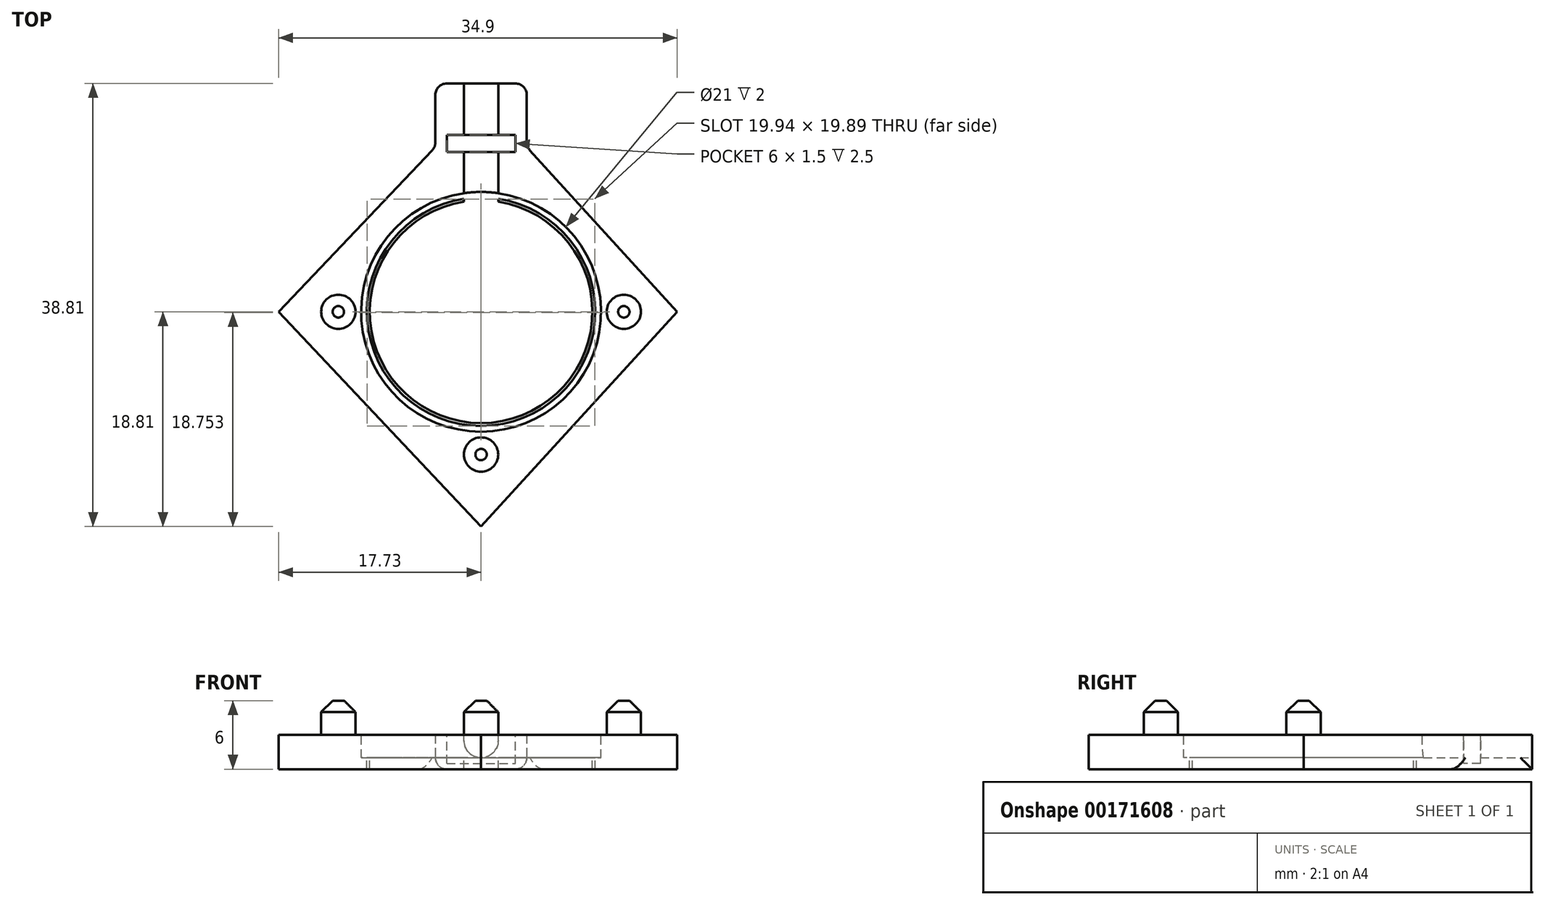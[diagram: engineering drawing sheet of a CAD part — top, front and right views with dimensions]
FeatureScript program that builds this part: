
annotation { "Feature Type Name" : "Feature", "Feature Type Description" : "" }
export const myFeature = defineFeature(function(context is Context, id is Id, definition is map)
    precondition{}
    {
        {
            var Q0;
            Q0=qCreatedBy(makeId("Top.planeOp"),FACE);
            var sketch = newSketch(context, id + "F0", { "sketchPlane" : qUnion([Q0])});
            skLineSegment(sketch, "E0.bottom", {"start": v(-4, 20) * mm, "end": v(4, 20) * mm});
            skLineSegment(sketch, "E0.left", {"start": v(-4, 20) * mm, "end": v(-4, 14.46) * mm});
            skLineSegment(sketch, "E0.right", {"start": v(4, 20) * mm, "end": v(4, 14.46) * mm});
            skLineSegment(sketch, "E1", {"start": v(-4, 14.46) * mm, "end": v(-17.73, 0) * mm});
            skLineSegment(sketch, "E2", {"start": v(4, 14.46) * mm, "end": v(17.17, 0) * mm});
            skLineSegment(sketch, "E3", {"start": v(0, 0) * mm, "end": v(0, -18.81) * mm});
            skLineSegment(sketch, "E4", {"start": v(0, -18.81) * mm, "end": v(-17.73, 0) * mm});
            skLineSegment(sketch, "E5", {"start": v(0, -18.81) * mm, "end": v(17.17, 0) * mm});
            skSolve(sketch);
        }
        {
            var Q0;
            Q0=qSketchRegion(id+"F0",true);
            extrude(context, id + "F1", {"entities" : qUnion([Q0]), "depth" : 3 * mm});
        }
        {
            var Q0;
            Q0=makeQuery(id+"F1.opExtrude","CAP_FACE",FACE,{"disambiguationData":[OSD([sQuery(id+"F0.wireOp",EDGE,"9GDV016W-EE9P-wzn8-Ccm6-bac6Yka38ORT"),sQuery(id+"F0.wireOp",EDGE,"E0.bottom"),sQuery(id+"F0.wireOp",EDGE,"E0.left"),sQuery(id+"F0.wireOp",EDGE,"E0.right")])],"isStart":false});
            var sketch = newSketch(context, id + "F2", { "sketchPlane" : qUnion([Q0])});
            skLineSegment(sketch, "E6.bottom", {"start": v(-1.5, 20) * mm, "end": v(1.5, 20) * mm});
            skLineSegment(sketch, "E6.left", {"start": v(-1.5, 20) * mm, "end": v(-1.5, 10.4) * mm});
            skLineSegment(sketch, "E6.right", {"start": v(1.5, 20) * mm, "end": v(1.5, 10.4) * mm});
            skArc(sketch, "E7", {"start": v(-1.5, 10.4) * mm, "mid": v(0, -10.5) * mm, "end": v(1.5, 10.4) * mm});
            skPoint(sketch, "E8.orphan", {"position": v(1.5, 8.67) * mm});
            skSolve(sketch);
        }
        {
            var Q0;
            Q0=qSketchRegion(id+"F2",true);
            extrude(context, id + "F3", {"entities" : qUnion([Q0]), "operationType" : NewBodyOperationType.REMOVE, "oppositeDirection" : true, "depth" : 2 * mm});
        }
        {
            var Q0;
            Q0=makeQuery(id+"F1.opExtrude","CAP_FACE",FACE,{"disambiguationData":[OSD([sQuery(id+"F0.wireOp",EDGE,"9GDV016W-EE9P-wzn8-Ccm6-bac6Yka38ORT"),sQuery(id+"F0.wireOp",EDGE,"E0.bottom"),sQuery(id+"F0.wireOp",EDGE,"E0.left"),sQuery(id+"F0.wireOp",EDGE,"E0.right")])],"isStart":false});
            var sketch = newSketch(context, id + "F4", { "sketchPlane" : qUnion([Q0])});
            skCircle(sketch, "E9", {"center": v(12.5, 0) * mm, "radius": 1.5 * mm});
            skCircle(sketch, "E10", {"center": v(-12.5, 0) * mm, "radius": 1.5 * mm});
            skCircle(sketch, "E11", {"center": v(0, -12.5) * mm, "radius": 1.5 * mm});
            skSolve(sketch);
        }
        {
            var Q0;
            Q0=qSketchRegion(id+"F4",true);
            extrude(context, id + "F5", {"entities" : qUnion([Q0]), "operationType" : NewBodyOperationType.ADD, "depth" : 3 * mm});
        }
        {
            var Q0;
            Q0=makeQuery(id+"F5.opExtrude","CAP_EDGE",EDGE,{"disambiguationData":[OSD([sQuery(id+"F4.wireOp",EDGE,"E10")])],"isStart":false});
            var Q1;
            Q1=makeQuery(id+"F5.opExtrude","CAP_EDGE",EDGE,{"disambiguationData":[OSD([sQuery(id+"F4.wireOp",EDGE,"E11")])],"isStart":false});
            var Q2;
            Q2=makeQuery(id+"F5.opExtrude","CAP_EDGE",EDGE,{"disambiguationData":[OSD([sQuery(id+"F4.wireOp",EDGE,"E9")])],"isStart":false});
            chamfer(context, id + "F6", {"entities" : qUnion([Q0, Q1, Q2]), "width" : 1 * mm, "tangentPropagation" : true});
        }
        {
            var Q0;
            Q0=makeQuery(id+"F1.opExtrude","CAP_EDGE",EDGE,{"disambiguationData":[OSD([sQuery(id+"F0.wireOp",EDGE,"E0.right")])],"isStart":true});
            var Q1;
            Q1=makeQuery(id+"F1.opExtrude","SWEPT_EDGE",EDGE,{"disambiguationData":[OSD([sQuery(id+"F0.wireOp",EDGE,"9GDV016W-EE9P-wzn8-Ccm6-bac6Yka38ORT"),sQuery(id+"F0.wireOp",EDGE,"E0.right")])]});
            var Q2;
            Q2=makeQuery(id+"F1.opExtrude","SWEPT_EDGE",EDGE,{"disambiguationData":[OSD([sQuery(id+"F0.wireOp",EDGE,"9GDV016W-EE9P-wzn8-Ccm6-bac6Yka38ORT"),sQuery(id+"F0.wireOp",EDGE,"E0.left")])]});
            var Q3;
            Q3=makeQuery(id+"F1.opExtrude","CAP_EDGE",EDGE,{"disambiguationData":[OSD([sQuery(id+"F0.wireOp",EDGE,"E0.left")])],"isStart":true});
            fillet(context, id + "F7", {"entities" : qUnion([Q0, Q1, Q2, Q3]), "radius" : 1 * mm, "tangentPropagation" : true, "allowEdgeOverflow" : false});
        }
        {
            var Q0;
            Q0=makeQuery(id+"F3.boolean.opBoolean","COPY",FACE,{"derivedFrom":makeQuery(id+"F3.opExtrude","CAP_FACE",FACE,{"disambiguationData":[OSD([sQuery(id+"F2.wireOp",EDGE,"E6.bottom"),sQuery(id+"F2.wireOp",EDGE,"E6.left"),sQuery(id+"F2.wireOp",EDGE,"E6.right"),sQuery(id+"F2.wireOp",EDGE,"E7")])],"isStart":false})});
            var sketch = newSketch(context, id + "F8", { "sketchPlane" : qUnion([Q0])});
            skArc(sketch, "E12", {"start": v(-1.5, 9.89) * mm, "mid": v(0, -10) * mm, "end": v(1.5, 9.89) * mm});
            skArc(sketch, "E13", {"start": v(-1.5, 9.63) * mm, "mid": v(0, -9.75) * mm, "end": v(1.5, 9.63) * mm});
            skLineSegment(sketch, "E14.left", {"start": v(-1.5, 9.89) * mm, "end": v(-1.5, 9.63) * mm});
            skLineSegment(sketch, "E14.right", {"start": v(1.5, 9.89) * mm, "end": v(1.5, 9.63) * mm});
            skPoint(sketch, "E15.orphan", {"position": v(1.5, 7.73) * mm});
            skSolve(sketch);
        }
        {
            var Q0;
            Q0=qSketchRegion(id+"F8",true);
            extrude(context, id + "F9", {"entities" : qUnion([Q0]), "operationType" : NewBodyOperationType.REMOVE, "endBound" : BoundingType.THROUGH_ALL, "oppositeDirection" : true, "depth" : 25 * mm});
        }
        {
            var Q0;
            Q0=makeQuery(id+"F3.boolean.opBoolean","COPY",EDGE,{"derivedFrom":makeQuery(id+"F3.opExtrude","CAP_EDGE",EDGE,{"disambiguationData":[OSD([sQuery(id+"F2.wireOp",EDGE,"E6.right")])],"isStart":false})});
            var Q1;
            Q1=makeQuery(id+"F3.boolean.opBoolean","COPY",EDGE,{"derivedFrom":makeQuery(id+"F3.opExtrude","CAP_EDGE",EDGE,{"disambiguationData":[OSD([sQuery(id+"F2.wireOp",EDGE,"E6.left")])],"isStart":false})});
            fillet(context, id + "F10", {"entities" : qUnion([Q0, Q1]), "radius" : 1.5 * mm, "tangentPropagation" : true, "allowEdgeOverflow" : false});
        }
        {
            var Q0;
            Q0=makeQuery(id+"F1.opExtrude","CAP_FACE",FACE,{"disambiguationData":[OSD([sQuery(id+"F0.wireOp",EDGE,"9GDV016W-EE9P-wzn8-Ccm6-bac6Yka38ORT"),sQuery(id+"F0.wireOp",EDGE,"E0.bottom"),sQuery(id+"F0.wireOp",EDGE,"E0.left"),sQuery(id+"F0.wireOp",EDGE,"E0.right")])],"isStart":false});
            var sketch = newSketch(context, id + "F11", { "sketchPlane" : qUnion([Q0])});
            skLineSegment(sketch, "E16.bottom", {"start": v(-3, 15.5) * mm, "end": v(3, 15.5) * mm});
            skLineSegment(sketch, "E16.top", {"start": v(-3, 14) * mm, "end": v(3, 14) * mm});
            skLineSegment(sketch, "E16.left", {"start": v(-3, 15.5) * mm, "end": v(-3, 14) * mm});
            skLineSegment(sketch, "E16.right", {"start": v(3, 15.5) * mm, "end": v(3, 14) * mm});
            skSolve(sketch);
        }
        {
            var Q0;
            Q0=qSketchRegion(id+"F11",true);
            extrude(context, id + "F12", {"entities" : qUnion([Q0]), "operationType" : NewBodyOperationType.REMOVE, "oppositeDirection" : true, "depth" : 2.5 * mm});
        }
    });
